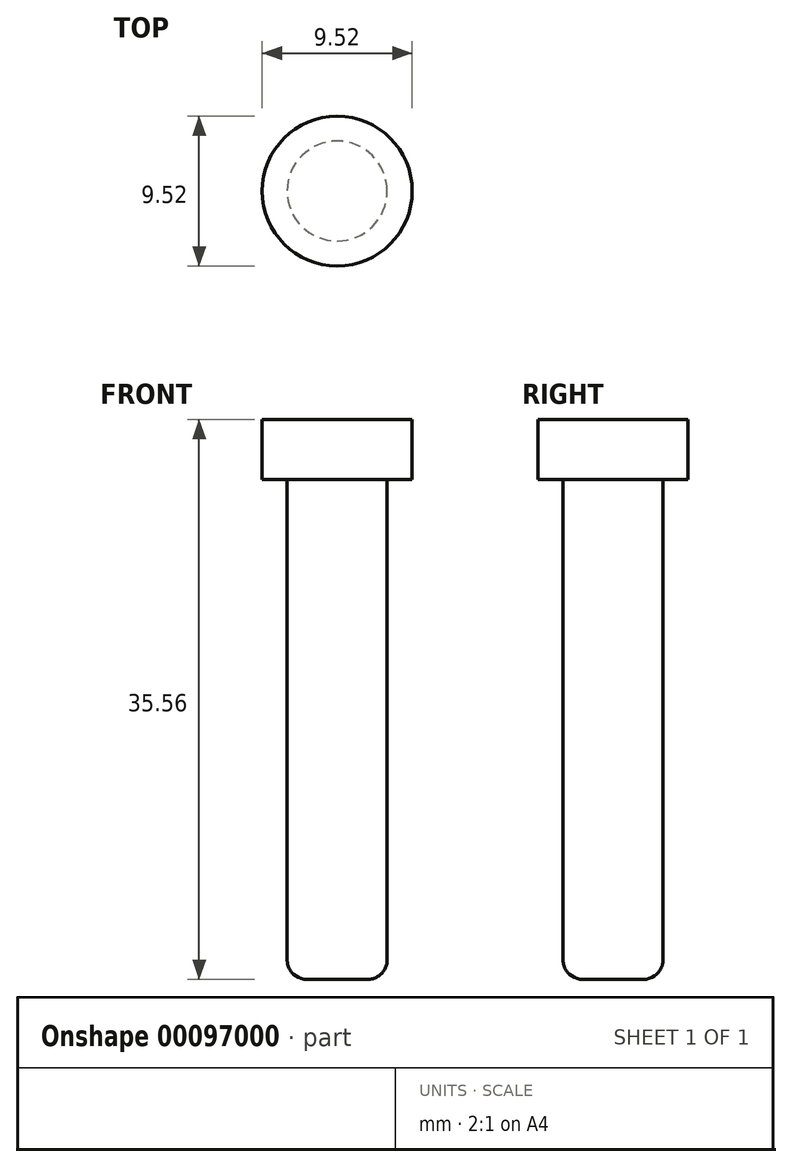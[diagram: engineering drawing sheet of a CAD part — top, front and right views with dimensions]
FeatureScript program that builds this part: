
annotation { "Feature Type Name" : "Feature", "Feature Type Description" : "" }
export const myFeature = defineFeature(function(context is Context, id is Id, definition is map)
    precondition{}
    {
        {
            var Q0;
            Q0=qCreatedBy(makeId("Top.planeOp"),FACE);
            var sketch = newSketch(context, id + "F0", { "sketchPlane" : qUnion([Q0])});
            skCircle(sketch, "E0", {"center": v(0, 0) * mm, "radius": 3.18 * mm});
            skSolve(sketch);
        }
        {
            var Q0;
            Q0 = qSketchRegion(id + "F0", true);
            extrude(context, id + "F1", {"entities" : qUnion([Q0]), "oppositeDirection" : true, "depth" : 35.56 * mm});
        }
        {
            var Q0;
            Q0=qCreatedBy(makeId("Top.planeOp"),FACE);
            var sketch = newSketch(context, id + "F2", { "sketchPlane" : qUnion([Q0])});
            skCircle(sketch, "E1", {"center": v(0, 0) * mm, "radius": 4.76 * mm});
            skSolve(sketch);
        }
        {
            var Q0;
            Q0 = qSketchRegion(id + "F2", true);
            extrude(context, id + "F3", {"entities" : qUnion([Q0]), "operationType" : NewBodyOperationType.ADD, "oppositeDirection" : true, "depth" : 3.81 * mm});
        }
        {
            var Q0;
            Q0=makeQuery(id+"F1.opExtrude","CAP_EDGE",EDGE,{"disambiguationData":[OSD([sQuery(id+"F0.wireOp",EDGE,"E0")])],"isStart":false});
            fillet(context, id + "F4", {"entities" : qUnion([Q0]), "radius" : 1.25 * mm, "tangentPropagation" : true, "allowEdgeOverflow" : false});
        }
    });
